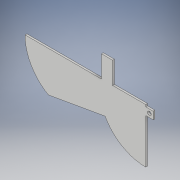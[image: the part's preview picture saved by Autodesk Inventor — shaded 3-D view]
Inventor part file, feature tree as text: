
AUTODESK INVENTOR PART (.ipt)
format: ipt  version: 2019 (Build 230136000, 136)  size: 141,824 bytes
history: native  units: in
note: dims shown in document units (in); Inventor stores cm internally (conversion verified against a paired STEP export)
features: extrude x3, sketch x3, projected_geometry x1
ambient origin geometry x8: Origin, YZ Plane, XZ Plane, XY Plane, X Axis, Y Axis, Z Axis, Center Point
bodies: Solid1 (feature_tree)
feature tree (7):
  extrude  "Extrusion1"  Depth=3.125in
  extrude  "Extrusion2"  Depth=4.0in
  extrude  "Extrusion3"  Depth=3.125in
  sketch  "Sketch1"  dims[d0=3.125in d1=2.706in]
  sketch  "Sketch2"  dims[d2=1.563in d3=4.0in]
  sketch  "Sketch3"  dims[d4=0.0687in d5=3.125in d6=3.0in d7=0.125in d9=0.0in d10=0.0in d11=1.928in d12=0.125in d13=0.0in d14=0.5in d15=0.5in d16=3.6361in d17=0.25in d18=3.25in d19=0.25in d20=0.125in d21=0.0in d22=0.75in d23=3.5in d25=1.8516in d26=2.4701in d27=0.125in d28=0.0in]
  projected_geometry  "Projected Loop1"
